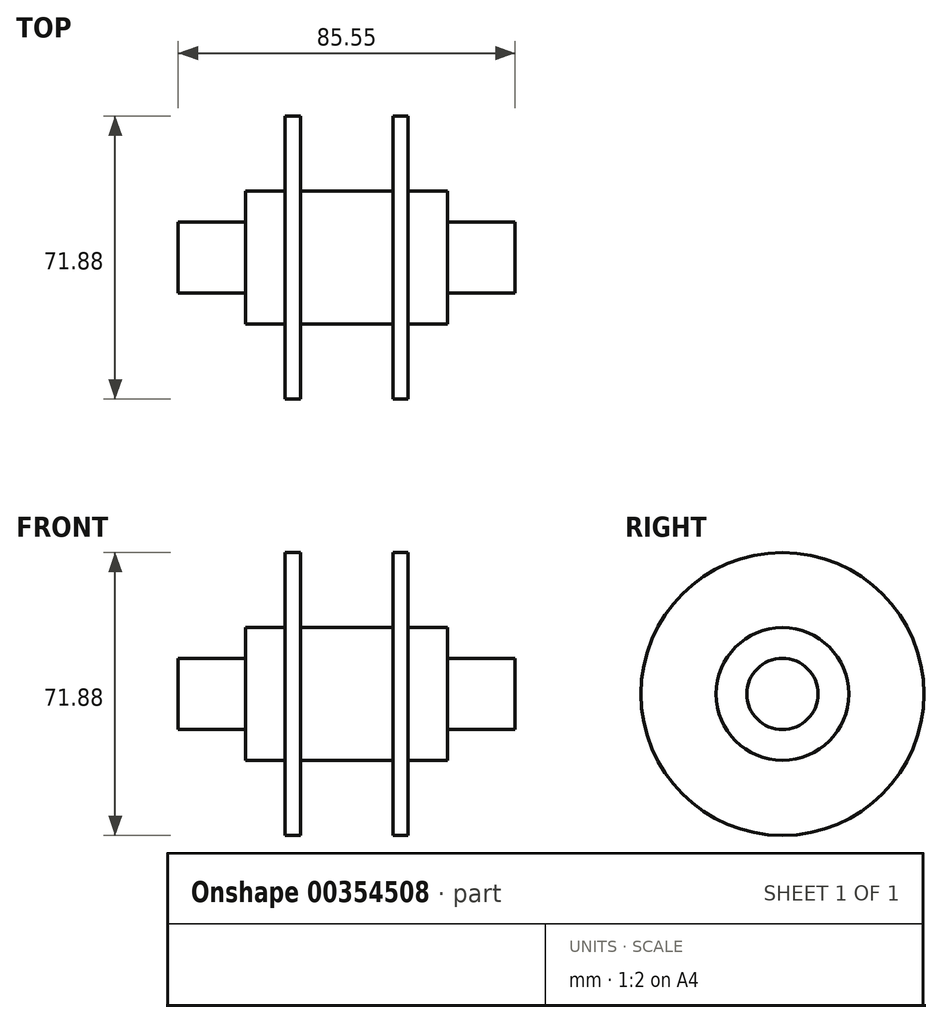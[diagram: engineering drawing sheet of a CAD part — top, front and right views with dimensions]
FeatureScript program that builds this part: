
annotation { "Feature Type Name" : "Feature", "Feature Type Description" : "" }
export const myFeature = defineFeature(function(context is Context, id is Id, definition is map)
    precondition{}
    {
        {
            var Q0;
            Q0=qCreatedBy(makeId("Front.planeOp"),FACE);
            var sketch = newSketch(context, id + "F0", { "sketchPlane" : qUnion([Q0])});
            skLineSegment(sketch, "E0.bottom", {"start": v(-4.24, 4.52) * mm, "end": v(-21.39, 4.52) * mm});
            skLineSegment(sketch, "E0.top", {"start": v(21.39, -4.52) * mm, "end": v(-21.39, -4.52) * mm});
            skLineSegment(sketch, "E0.left", {"start": v(21.39, 4.52) * mm, "end": v(21.39, -4.52) * mm});
            skLineSegment(sketch, "E0.right", {"start": v(-21.39, 4.52) * mm, "end": v(-21.39, -4.52) * mm});
            skLineSegment(sketch, "E1", {"start": v(21.39, 4.52) * mm, "end": v(21.39, 12.34) * mm});
            skLineSegment(sketch, "E2", {"start": v(21.39, 12.34) * mm, "end": v(9.66, 12.34) * mm});
            skLineSegment(sketch, "E3", {"start": v(-4.24, 12.34) * mm, "end": v(-4.24, 4.52) * mm});
            skLineSegment(sketch, "E4", {"start": v(5.75, 12.34) * mm, "end": v(5.75, 31.42) * mm});
            skLineSegment(sketch, "E5", {"start": v(5.75, 31.42) * mm, "end": v(9.66, 31.42) * mm});
            skLineSegment(sketch, "E6", {"start": v(9.66, 31.42) * mm, "end": v(9.66, 12.34) * mm});
            skLineSegment(sketch, "E7.trimOffspring", {"start": v(5.75, 12.34) * mm, "end": v(-4.24, 12.34) * mm});
            skLineSegment(sketch, "E8.MirrorCS", {"start": v(21.39, -4.52) * mm, "end": v(64.16, -4.52) * mm});
            skLineSegment(sketch, "E9.MirrorCS", {"start": v(21.39, 12.34) * mm, "end": v(33.12, 12.34) * mm});
            skLineSegment(sketch, "E10.MirrorCS", {"start": v(33.12, 31.42) * mm, "end": v(33.12, 12.34) * mm});
            skLineSegment(sketch, "E11.MirrorCS", {"start": v(37.03, 31.42) * mm, "end": v(33.12, 31.42) * mm});
            skLineSegment(sketch, "E12.MirrorCS", {"start": v(37.03, 12.34) * mm, "end": v(37.03, 31.42) * mm});
            skLineSegment(sketch, "E13.MirrorCS", {"start": v(37.03, 12.34) * mm, "end": v(47.02, 12.34) * mm});
            skLineSegment(sketch, "E14.MirrorCS", {"start": v(47.02, 12.34) * mm, "end": v(47.02, 4.52) * mm});
            skLineSegment(sketch, "E15.MirrorCS", {"start": v(47.02, 4.52) * mm, "end": v(64.16, 4.52) * mm});
            skLineSegment(sketch, "E16.MirrorCS", {"start": v(64.16, 4.52) * mm, "end": v(64.16, -4.52) * mm});
            skSolve(sketch);
        }
        {
            var Q0;
            Q0=makeQuery(id+"F0.imprint","IMPRINT",FACE,{"disambiguationData":[TD([[makeQuery(id+"F0.imprint","IMPRINT",EDGE,{"derivedFrom":sQuery(id+"F0.wireOp",EDGE,"E0.bottom")}),1.0]])]});
            var Q1;
            Q1=sQuery(id+"F0.wireOp",EDGE,"E0.top");
            revolve(context, id + "F1", {"entities" : qUnion([Q0]), "axis" : qUnion([Q1]), "revolveType" : RevolveType.FULL});
        }
        {
            var Q0;
            Q0=makeQuery(id+"F1.opRevolve","SWEPT_BODY",BODY,{"disambiguationData":[OSD([sQuery(id+"F0.wireOp",EDGE,"E0.bottom"),sQuery(id+"F0.wireOp",EDGE,"E0.top"),sQuery(id+"F0.wireOp",EDGE,"E0.left"),sQuery(id+"F0.wireOp",EDGE,"E0.right"),sQuery(id+"F0.wireOp",EDGE,"E1"),sQuery(id+"F0.wireOp",EDGE,"E2"),sQuery(id+"F0.wireOp",EDGE,"E3"),sQuery(id+"F0.wireOp",EDGE,"E4"),sQuery(id+"F0.wireOp",EDGE,"E5"),sQuery(id+"F0.wireOp",EDGE,"E6"),sQuery(id+"F0.wireOp",EDGE,"E7.trimOffspring")])]});
            var Q1;
            Q1=makeQuery(id+"F1.opRevolve","SWEPT_FACE",FACE,{"disambiguationData":[OSD([sQuery(id+"F0.wireOp",EDGE,"E0.left"),sQuery(id+"F0.wireOp",EDGE,"E1")])]});
            mirror(context, id + "F2", {"operationType" : NewBodyOperationType.ADD, "entities" : qUnion([Q0]), "mirrorPlane" : qUnion([Q1])});
        }
    });
